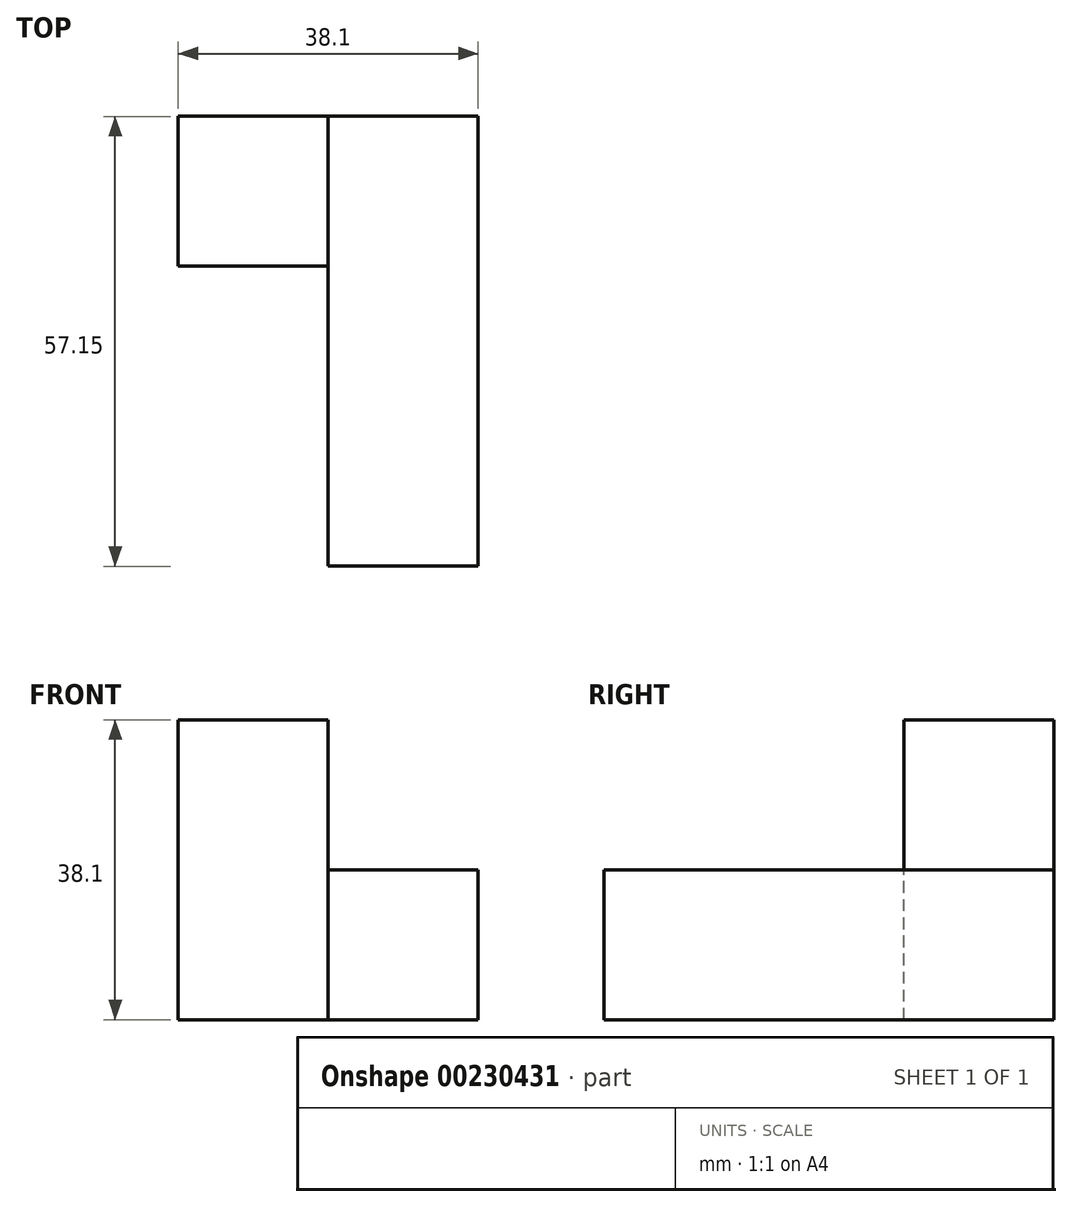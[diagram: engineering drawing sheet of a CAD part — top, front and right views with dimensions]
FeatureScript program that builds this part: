
annotation { "Feature Type Name" : "Feature", "Feature Type Description" : "" }
export const myFeature = defineFeature(function(context is Context, id is Id, definition is map)
    precondition{}
    {
        {
            var Q0;
            Q0=qCreatedBy(makeId("Top.planeOp"),FACE);
            var sketch = newSketch(context, id + "F0", { "sketchPlane" : qUnion([Q0])});
            skLineSegment(sketch, "E0.bottom", {"start": v(-37.97, 44.6) * mm, "end": v(-18.92, 44.6) * mm});
            skLineSegment(sketch, "E0.top", {"start": v(-37.97, -12.56) * mm, "end": v(-18.92, -12.56) * mm});
            skLineSegment(sketch, "E0.left", {"start": v(-37.97, 44.6) * mm, "end": v(-37.97, -12.56) * mm});
            skLineSegment(sketch, "E0.right", {"start": v(-18.92, 44.6) * mm, "end": v(-18.92, -12.56) * mm});
            skSolve(sketch);
        }
        {
            var Q0;
            Q0=makeQuery(id+"F0.imprint","IMPRINT",FACE,{"disambiguationData":[TD([[makeQuery(id+"F0.imprint","IMPRINT",EDGE,{"derivedFrom":sQuery(id+"F0.wireOp",EDGE,"E0.bottom")}),-1.0]])]});
            extrude(context, id + "F1", {"entities" : qUnion([Q0]), "depth" : 19.05 * mm});
        }
        {
            var Q0;
            Q0=makeQuery(id+"F1.opExtrude","SWEPT_FACE",FACE,{"disambiguationData":[OSD([sQuery(id+"F0.wireOp",EDGE,"E0.left")])]});
            var sketch = newSketch(context, id + "F2", { "sketchPlane" : qUnion([Q0])});
            skLineSegment(sketch, "E1.bottom", {"start": v(-44.6, 0) * mm, "end": v(-25.54, 0) * mm});
            skLineSegment(sketch, "E1.top", {"start": v(-44.6, 19.05) * mm, "end": v(-25.54, 19.05) * mm});
            skLineSegment(sketch, "E1.left", {"start": v(-44.6, 0) * mm, "end": v(-44.6, 19.05) * mm});
            skLineSegment(sketch, "E1.right", {"start": v(-25.54, 0) * mm, "end": v(-25.54, 19.05) * mm});
            skSolve(sketch);
        }
        {
            var Q0;
            Q0=makeQuery(id+"F2.imprint","IMPRINT",FACE,{"disambiguationData":[TD([[makeQuery(id+"F2.imprint","IMPRINT",EDGE,{"derivedFrom":sQuery(id+"F2.wireOp",EDGE,"E1.bottom")}),1.0]])]});
            extrude(context, id + "F3", {"entities" : qUnion([Q0]), "operationType" : NewBodyOperationType.ADD, "depth" : 19.05 * mm});
        }
        {
            var Q0;
            Q0=makeQuery(id+"F3.boolean.opBoolean","MERGE",FACE,{"derivedFrom":[makeQuery(id+"F1.opExtrude","CAP_FACE",FACE,{"disambiguationData":[OSD([sQuery(id+"F0.wireOp",EDGE,"E0.bottom"),sQuery(id+"F0.wireOp",EDGE,"E0.top"),sQuery(id+"F0.wireOp",EDGE,"E0.left"),sQuery(id+"F0.wireOp",EDGE,"E0.right")])],"isStart":false}),makeQuery(id+"F3.opExtrude","SWEPT_FACE",FACE,{"disambiguationData":[OSD([sQuery(id+"F2.wireOp",EDGE,"E1.top")])]})]});
            var sketch = newSketch(context, id + "F4", { "sketchPlane" : qUnion([Q0])});
            skLineSegment(sketch, "E2.bottom", {"start": v(-57.02, 44.6) * mm, "end": v(-37.97, 44.6) * mm});
            skLineSegment(sketch, "E2.top", {"start": v(-57.02, 25.54) * mm, "end": v(-37.97, 25.54) * mm});
            skLineSegment(sketch, "E2.left", {"start": v(-57.02, 44.6) * mm, "end": v(-57.02, 25.54) * mm});
            skLineSegment(sketch, "E2.right", {"start": v(-37.97, 44.6) * mm, "end": v(-37.97, 25.54) * mm});
            skSolve(sketch);
        }
        {
            var Q0;
            Q0 = qSketchRegion(id + "F4", true);
            extrude(context, id + "F5", {"entities" : qUnion([Q0]), "operationType" : NewBodyOperationType.ADD, "depth" : 19.05 * mm});
        }
    });
